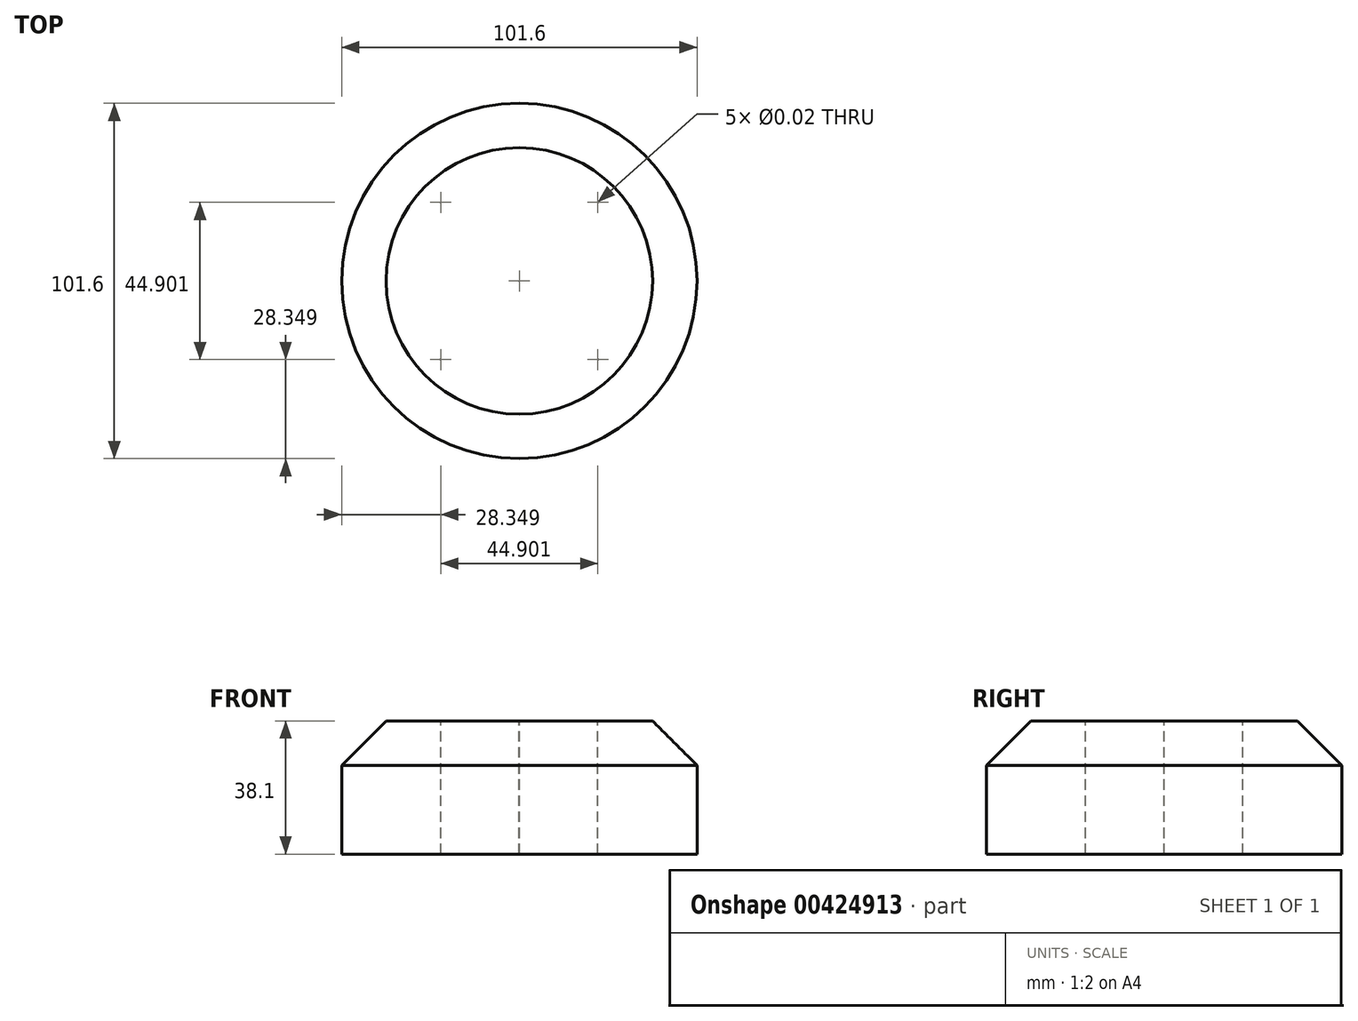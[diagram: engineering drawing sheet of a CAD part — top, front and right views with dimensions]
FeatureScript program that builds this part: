
annotation { "Feature Type Name" : "Feature", "Feature Type Description" : "" }
export const myFeature = defineFeature(function(context is Context, id is Id, definition is map)
    precondition{}
    {
        {
            var Q0;
            Q0=qCreatedBy(makeId("Top.planeOp"),FACE);
            var sketch = newSketch(context, id + "F0", { "sketchPlane" : qUnion([Q0])});
            skCircle(sketch, "E0", {"center": v(0, 0) * mm, "radius": 50.8 * mm});
            skSolve(sketch);
        }
        {
            var Q0;
            Q0 = qSketchRegion(id + "F0", true);
            extrude(context, id + "F1", {"entities" : qUnion([Q0]), "depth" : 38.1 * mm, "symmetric" : true});
        }
        {
            var Q0;
            Q0=makeQuery(id+"F1.opExtrude","CAP_EDGE",EDGE,{"disambiguationData":[OSD([sQuery(id+"F0.wireOp",EDGE,"E0")])],"isStart":false});
            chamfer(context, id + "F2", {"entities" : qUnion([Q0]), "width" : 12.7 * mm, "tangentPropagation" : true});
        }
        {
            var Q0;
            Q0=makeQuery(id+"F1.opExtrude","CAP_FACE",FACE,{"disambiguationData":[OSD([sQuery(id+"F0.wireOp",EDGE,"E0")])],"isStart":true});
            var sketch = newSketch(context, id + "F3", { "sketchPlane" : qUnion([Q0])});
            skCircle(sketch, "E1", {"center": v(0, 0) * mm, "radius": 31.75 * mm, "construction": true});
            skLineSegment(sketch, "E2", {"start": v(0, 31.75) * mm, "end": v(0, 0) * mm, "construction": true});
            skPoint(sketch, "E3", {"position": v(-22.45, 22.45) * mm});
            skPoint(sketch, "E4.1.0", {"position": v(-22.45, -22.45) * mm});
            skPoint(sketch, "E4.2.0", {"position": v(22.45, -22.45) * mm});
            skPoint(sketch, "E4.3.0", {"position": v(22.45, 22.45) * mm});
            skLineSegment(sketch, "E5", {"start": v(0, 0) * mm, "end": v(-22.45, 22.45) * mm, "construction": true});
            skSolve(sketch);
        }
        {
            var Q0;
            Q0=sQuery(id+"F3.wireOp",VERTEX,"E3");
            var Q1;
            Q1=sQuery(id+"F3.wireOp",VERTEX,"E4.1.0");
            var Q2;
            Q2=sQuery(id+"F3.wireOp",VERTEX,"E4.2.0");
            var Q3;
            Q3=sQuery(id+"F3.wireOp",VERTEX,"E4.3.0");
            var Q4;
            Q4=makeQuery(id+"F1.opExtrude","SWEPT_BODY",BODY,{"disambiguationData":[OSD([sQuery(id+"F0.wireOp",EDGE,"E0")])]});
            hole(context, id + "F4", {"style" : HoleStyle.SIMPLE, "endStyle" : HoleEndStyle.THROUGH, "standardTappedOrClearance" : lookupTablePath({ "standard" : "ANSI", "size" : "1/2 (0.5)", "type" : "Drilled" }), "standardBlindInLast" : lookupTablePath({ "standard" : "ANSI", "size" : "1/2", "type" : "Drilled" }), "holeDiameter" : 1 / 50.8 * mm, "isTappedThrough" : true, "tappedDepth" : 14.3 * mm, "tapClearance" : 3, "locations" : qUnion([Q0, Q1, Q2, Q3]), "scope" : qUnion([Q4]), "startStyle" : HoleStartStyle.SKETCH});
        }
        {
            var Q0;
            Q0=sQuery(id+"F3.wireOp",VERTEX,"E1.center");
            var Q1;
            Q1=makeQuery(id+"F1.opExtrude","SWEPT_BODY",BODY,{"disambiguationData":[OSD([sQuery(id+"F0.wireOp",EDGE,"E0")])]});
            hole(context, id + "F5", {"style" : HoleStyle.SIMPLE, "endStyle" : HoleEndStyle.THROUGH, "standardTappedOrClearance" : lookupTablePath({ "standard" : "ANSI", "size" : "5/8 (0.62)", "type" : "Drilled" }), "standardBlindInLast" : lookupTablePath({ "standard" : "ANSI", "size" : "5/8", "type" : "Drilled" }), "holeDiameter" : 5 / 203.2 * mm, "isTappedThrough" : true, "tappedDepth" : 14.3 * mm, "tapClearance" : 3, "locations" : qUnion([Q0]), "scope" : qUnion([Q1]), "startStyle" : HoleStartStyle.SKETCH});
        }
    });
